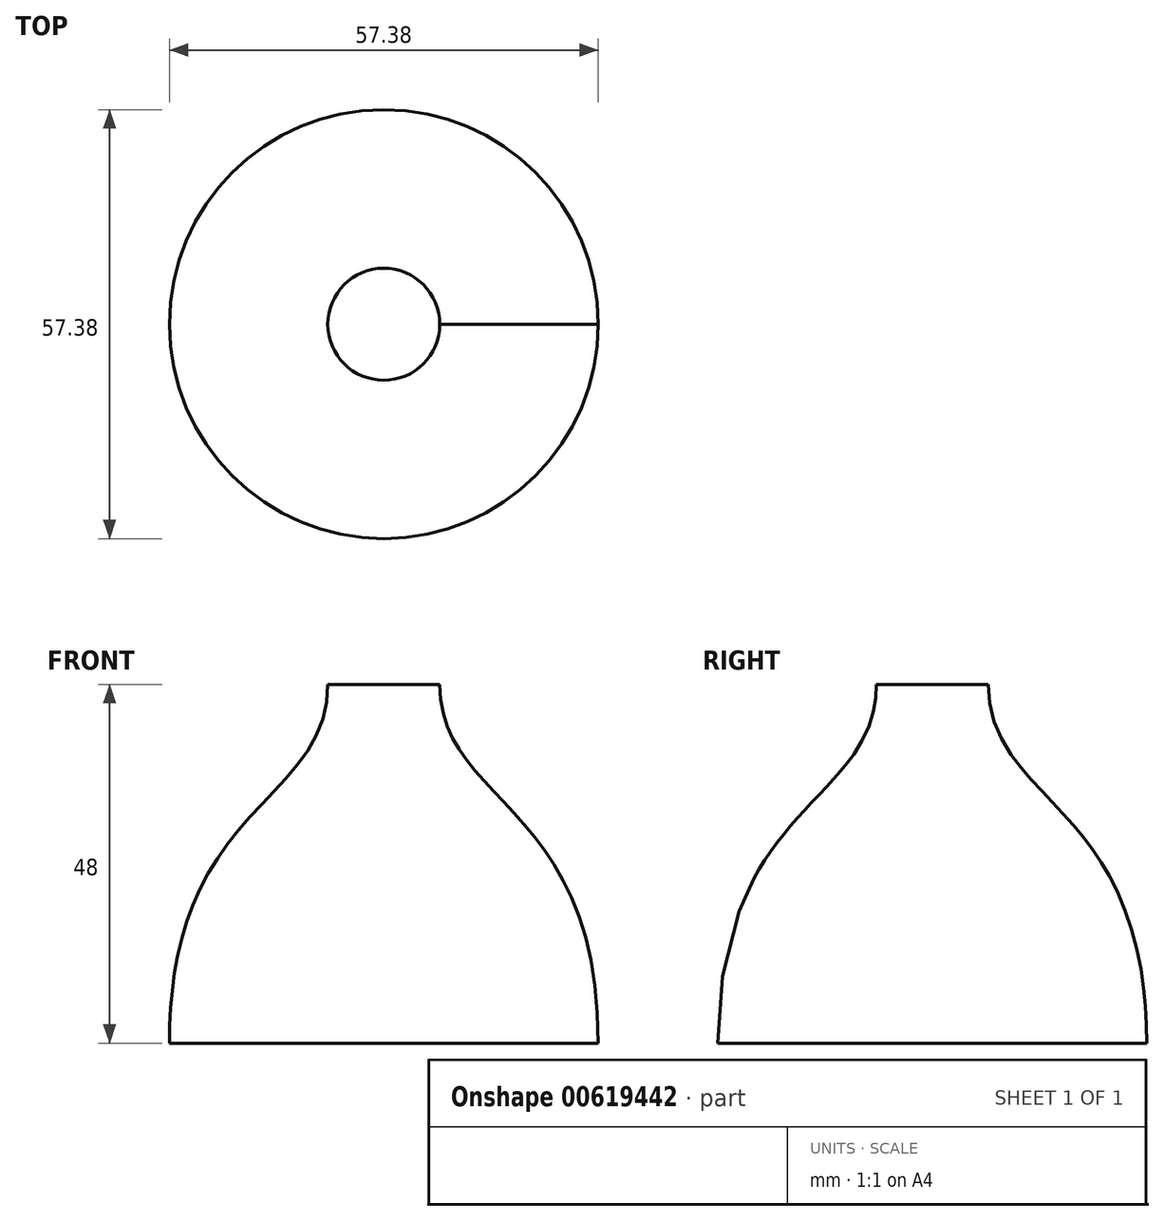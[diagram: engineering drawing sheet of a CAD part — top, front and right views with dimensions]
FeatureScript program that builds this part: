
annotation { "Feature Type Name" : "Feature", "Feature Type Description" : "" }
export const myFeature = defineFeature(function(context is Context, id is Id, definition is map)
    precondition{}
    {
        {
            var Q0;
            Q0=qCreatedBy(makeId("Top.planeOp"),FACE);
            var sketch = newSketch(context, id + "F0", { "sketchPlane" : qUnion([Q0])});
            skCircle(sketch, "E0", {"center": v(0, 0) * mm, "radius": 28.7 * mm});
            skSolve(sketch);
        }
        {
            var Q0;
            Q0=qCreatedBy(makeId("Top.planeOp"),FACE);
            cPlane(context, id + "F1", {"entities" : qUnion([Q0]), "cplaneType" : CPlaneType.OFFSET, "offset" : 48 * mm, "width" : 150 * mm, "height" : 150 * mm});
        }
        {
            var Q0;
            Q0=qCreatedBy(id+"F1.planeOp",FACE);
            var sketch = newSketch(context, id + "F2", { "sketchPlane" : qUnion([Q0])});
            skCircle(sketch, "E1", {"center": v(0, 0) * mm, "radius": 7.5 * mm});
            skSolve(sketch);
        }
        {
            var Q0;
            Q0=qCreatedBy(makeId("Top.planeOp"),FACE);
            cPlane(context, id + "F3", {"entities" : qUnion([Q0]), "cplaneType" : CPlaneType.OFFSET, "offset" : 25 * mm, "width" : 150 * mm, "height" : 150 * mm});
        }
        {
            var Q0;
            Q0=qCreatedBy(id+"F3.planeOp",FACE);
            var sketch = newSketch(context, id + "F4", { "sketchPlane" : qUnion([Q0])});
            skCircle(sketch, "E2", {"center": v(0, 0) * mm, "radius": 18.48 * mm});
            skSolve(sketch);
        }
        {
            var Q0;
            Q0=makeQuery(id+"F0.imprint","IMPRINT",FACE,{"disambiguationData":[TD([[makeQuery(id+"F0.imprint","IMPRINT",EDGE,{"derivedFrom":sQuery(id+"F0.wireOp",EDGE,"E0")}),1.0]])]});
            var Q1;
            Q1=makeQuery(id+"F2.imprint","IMPRINT",FACE,{"disambiguationData":[TD([[makeQuery(id+"F2.imprint","IMPRINT",EDGE,{"derivedFrom":sQuery(id+"F2.wireOp",EDGE,"E1")}),1.0]])]});
            var Q2;
            Q2=sQuery(id+"F4.wireOp",EDGE,"E2");
            loft(context, id + "F5", {"startCondition" : LoftEndDerivativeType.NORMAL_TO_PROFILE, "startMagnitude" : 2, "endCondition" : LoftEndDerivativeType.NORMAL_TO_PROFILE, "endMagnitude" : 1, "sheetProfilesArray" : [{ "sheetProfileEntities" : qUnion([Q0]) }, { "sheetProfileEntities" : qUnion([Q1]) }], "guidesArray" : [{ "guideEntities" : qUnion([Q2]), "guideDerivativeType" : LoftGuideDerivativeType.DEFAULT, "guideDerivativeMagnitude" : 1 }]});
        }
    });
